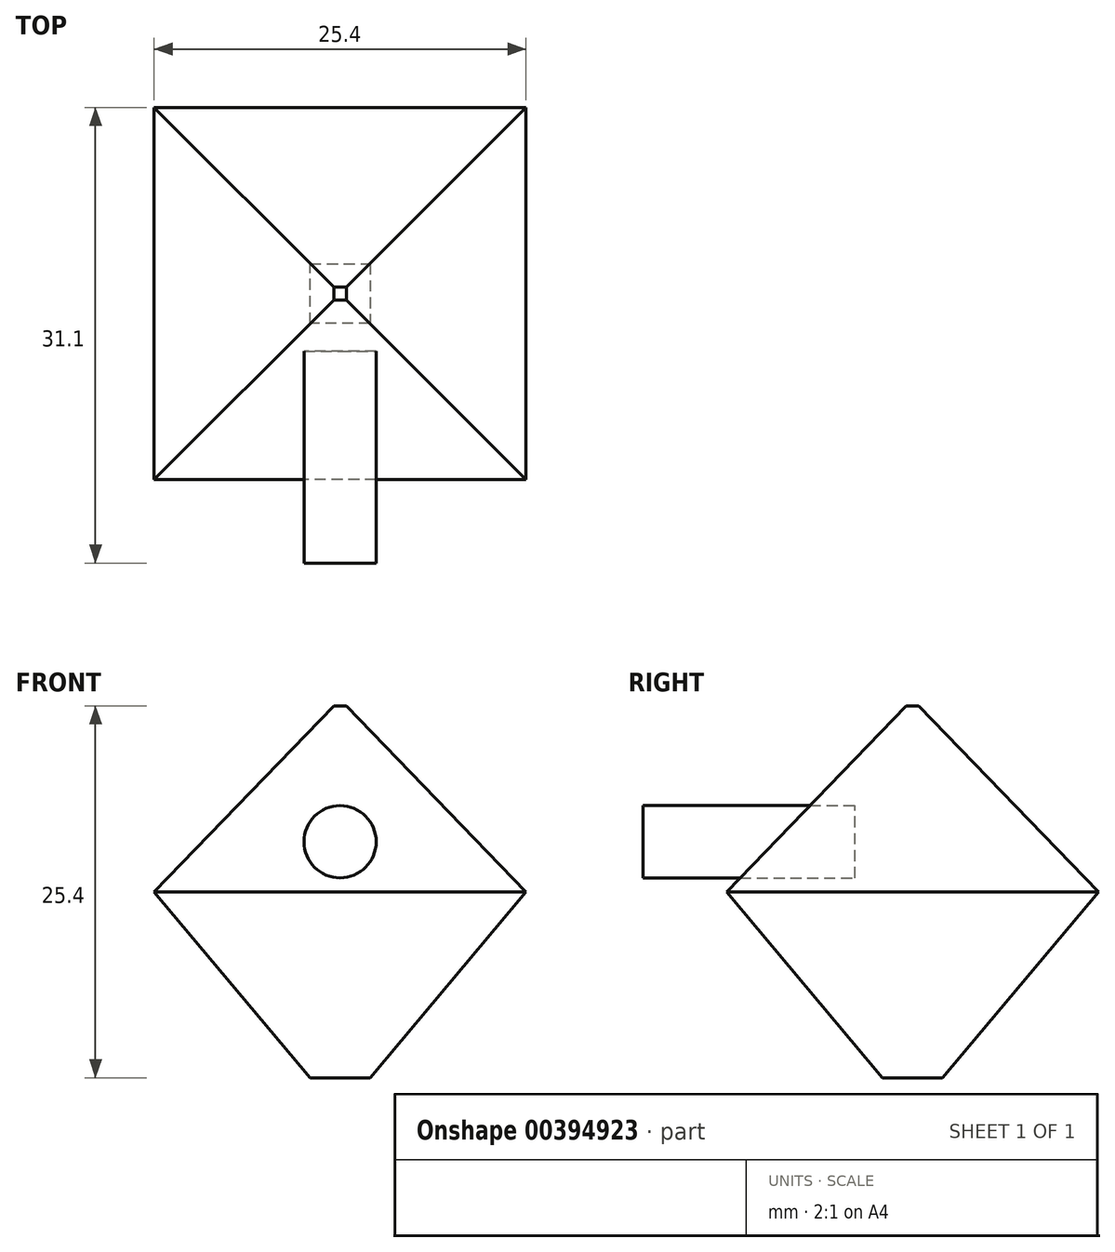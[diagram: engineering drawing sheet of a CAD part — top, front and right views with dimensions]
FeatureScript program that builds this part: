
annotation { "Feature Type Name" : "Feature", "Feature Type Description" : "" }
export const myFeature = defineFeature(function(context is Context, id is Id, definition is map)
    precondition{}
    {
        {
            var Q0;
            Q0=qCreatedBy(makeId("Top.planeOp"),FACE);
            var sketch = newSketch(context, id + "F0", { "sketchPlane" : qUnion([Q0])});
            skLineSegment(sketch, "E0.bottom", {"start": v(-12.7, 12.7) * mm, "end": v(12.7, 12.7) * mm});
            skLineSegment(sketch, "E0.top", {"start": v(-12.7, -12.7) * mm, "end": v(12.7, -12.7) * mm});
            skLineSegment(sketch, "E0.left", {"start": v(-12.7, 12.7) * mm, "end": v(-12.7, -12.7) * mm});
            skLineSegment(sketch, "E0.right", {"start": v(12.7, 12.7) * mm, "end": v(12.7, -12.7) * mm});
            skPoint(sketch, "E0.middle", {"position": v(0, 0) * mm});
            skSolve(sketch);
        }
        {
            var Q0;
            Q0=makeQuery(id+"F0.imprint","IMPRINT",FACE,{"disambiguationData":[TD([[makeQuery(id+"F0.imprint","IMPRINT",EDGE,{"derivedFrom":sQuery(id+"F0.wireOp",EDGE,"E0.bottom")}),-1.0]])]});
            extrude(context, id + "F1", {"entities" : qUnion([Q0]), "depth" : 12.7 * mm, "hasDraft" : true, "draftAngle" : 44 * degree, "draftPullDirection" : true, "hasSecondDirection" : true, "secondDirectionOppositeDirection" : true, "secondDirectionDepth" : 12.7 * mm, "hasSecondDirectionDraft" : true, "secondDirectionDraftAngle" : 40 * degree, "secondDirectionDraftPullDirection" : true});
        }
        {
            var Q0;
            Q0=qCreatedBy(makeId("Top.planeOp"),FACE);
            var sketch = newSketch(context, id + "F2", { "sketchPlane" : qUnion([Q0])});
            skLineSegment(sketch, "E1.bottom", {"start": v(-4.04, 3.92) * mm, "end": v(4.04, 3.92) * mm});
            skLineSegment(sketch, "E1.top", {"start": v(-4.04, -3.92) * mm, "end": v(4.04, -3.92) * mm});
            skLineSegment(sketch, "E1.left", {"start": v(-4.04, 3.92) * mm, "end": v(-4.04, -3.92) * mm});
            skLineSegment(sketch, "E1.right", {"start": v(4.04, 3.92) * mm, "end": v(4.04, -3.92) * mm});
            skPoint(sketch, "E1.middle", {"position": v(0, 0) * mm});
            skSolve(sketch);
        }
        {
            var Q0;
            Q0=sQuery(id+"F2.wireOp",EDGE,"E1.top");
            extrude(context, id + "F3", {"bodyType" : ToolBodyType.SURFACE, "surfaceEntities" : qUnion([Q0]), "depth" : 7.11 * mm});
        }
        {
            var Q0;
            Q0=makeQuery(id+"F3.opExtrude","SWEPT_FACE",FACE,{"disambiguationData":[OSD([sQuery(id+"F2.wireOp",EDGE,"E1.top")])]});
            var sketch = newSketch(context, id + "F4", { "sketchPlane" : qUnion([Q0])});
            skCircle(sketch, "E2", {"center": v(0, 3.42) * mm, "radius": 2.47 * mm});
            skSolve(sketch);
        }
        {
            var Q0;
            Q0=makeQuery(id+"F4.imprint","IMPRINT",FACE,{"disambiguationData":[TD([[makeQuery(id+"F4.imprint","IMPRINT",EDGE,{"derivedFrom":sQuery(id+"F4.wireOp",EDGE,"E2")}),1.0]])]});
            extrude(context, id + "F5", {"entities" : qUnion([Q0]), "depth" : 14.48 * mm});
        }
    });
